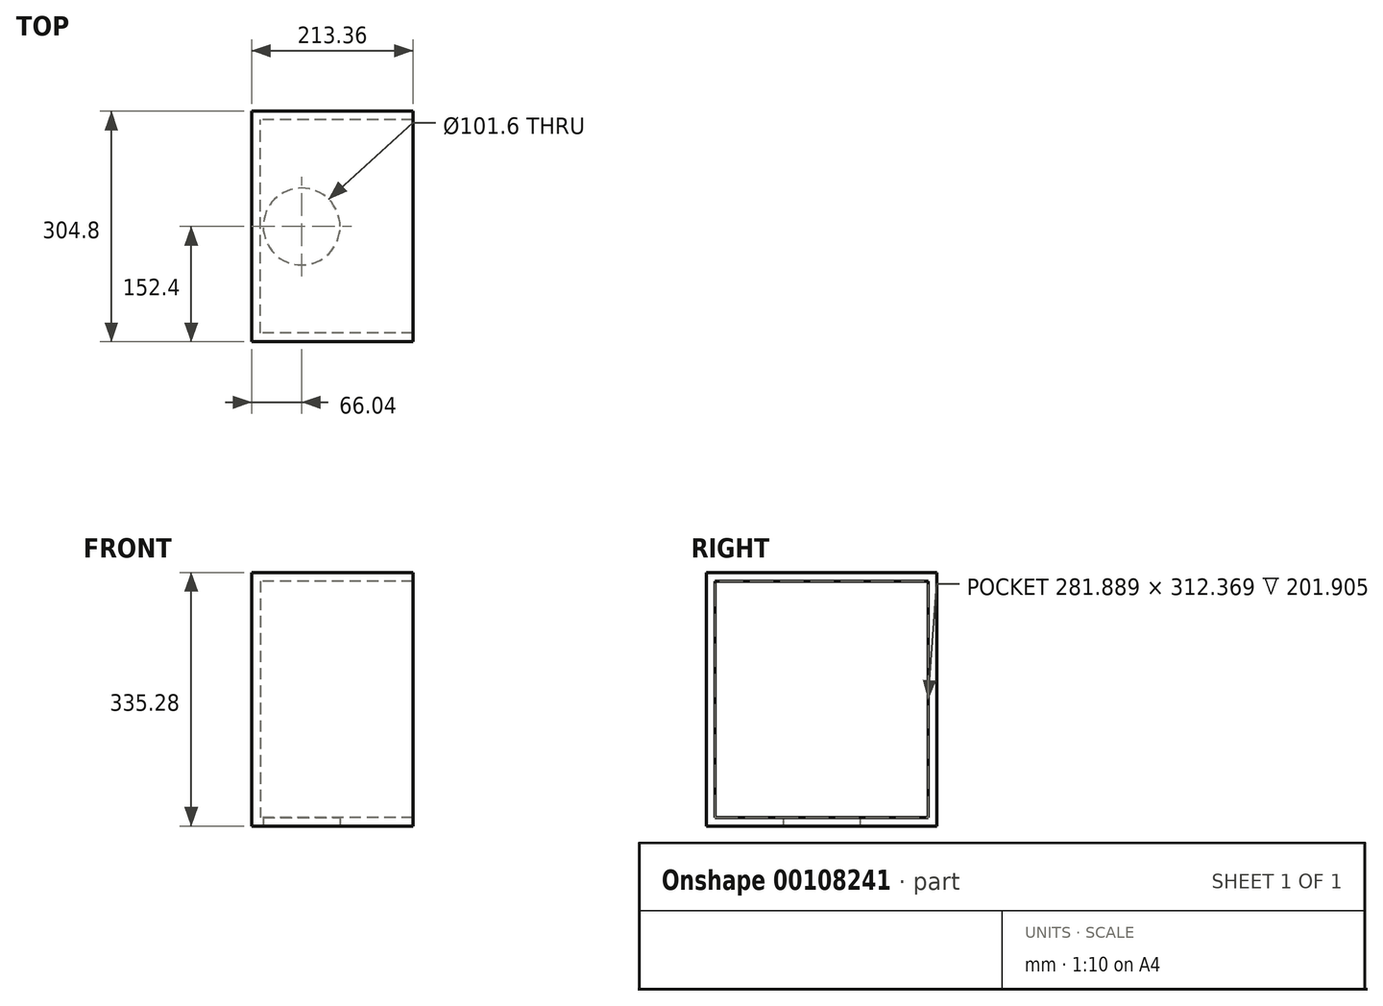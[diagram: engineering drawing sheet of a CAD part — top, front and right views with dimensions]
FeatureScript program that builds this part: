
annotation { "Feature Type Name" : "Feature", "Feature Type Description" : "" }
export const myFeature = defineFeature(function(context is Context, id is Id, definition is map)
    precondition{}
    {
        {
            var Q0;
            Q0=qCreatedBy(makeId("Front.planeOp"),FACE);
            var sketch = newSketch(context, id + "F0", { "sketchPlane" : qUnion([Q0])});
            skLineSegment(sketch, "E0.bottom", {"start": v(106.68, 167.64) * mm, "end": v(-106.68, 167.64) * mm});
            skLineSegment(sketch, "E0.top", {"start": v(106.68, -167.64) * mm, "end": v(-106.68, -167.64) * mm});
            skLineSegment(sketch, "E0.left", {"start": v(106.68, 167.64) * mm, "end": v(106.68, -167.64) * mm});
            skLineSegment(sketch, "E0.right", {"start": v(-106.68, 167.64) * mm, "end": v(-106.68, -167.64) * mm});
            skPoint(sketch, "E0.middle", {"position": v(0, 0) * mm});
            skSolve(sketch);
        }
        {
            var Q0;
            Q0=makeQuery(id+"F0.imprint","IMPRINT",FACE,{"disambiguationData":[TD([[makeQuery(id+"F0.imprint","IMPRINT",EDGE,{"derivedFrom":sQuery(id+"F0.wireOp",EDGE,"E0.bottom")}),1.0]])]});
            extrude(context, id + "F1", {"entities" : qUnion([Q0]), "depth" : 304.8 * mm});
        }
        {
            var Q0;
            Q0=makeQuery(id+"F1.opExtrude","SWEPT_FACE",FACE,{"disambiguationData":[OSD([sQuery(id+"F0.wireOp",EDGE,"E0.left")])]});
            shell(context, id + "F2", {"entities" : qUnion([Q0]), "thickness" : 11.46 * mm});
        }
        {
            var Q0;
            Q0=makeQuery(id+"F1.opExtrude","SWEPT_FACE",FACE,{"disambiguationData":[OSD([sQuery(id+"F0.wireOp",EDGE,"E0.top")])]});
            var sketch = newSketch(context, id + "F3", { "sketchPlane" : qUnion([Q0])});
            skCircle(sketch, "E1", {"center": v(-40.64, 152.4) * mm, "radius": 50.8 * mm});
            skPoint(sketch, "E2", {"position": v(-106.68, 152.4) * mm});
            skSolve(sketch);
        }
        {
            var Q0;
            Q0 = qSketchRegion(id + "F3", true);
            var Q1;
            Q1=makeQuery(id+"F2.opShell","OFFSET_FACE",FACE,{"disambiguationData":[OSD([sQuery(id+"F0.wireOp",EDGE,"E0.top")])]});
            extrude(context, id + "F4", {"entities" : qUnion([Q0]), "operationType" : NewBodyOperationType.REMOVE, "endBound" : BoundingType.UP_TO_SURFACE, "oppositeDirection" : true, "endBoundEntityFace" : qUnion([Q1]), "depth" : 30.48 * mm});
        }
    });
